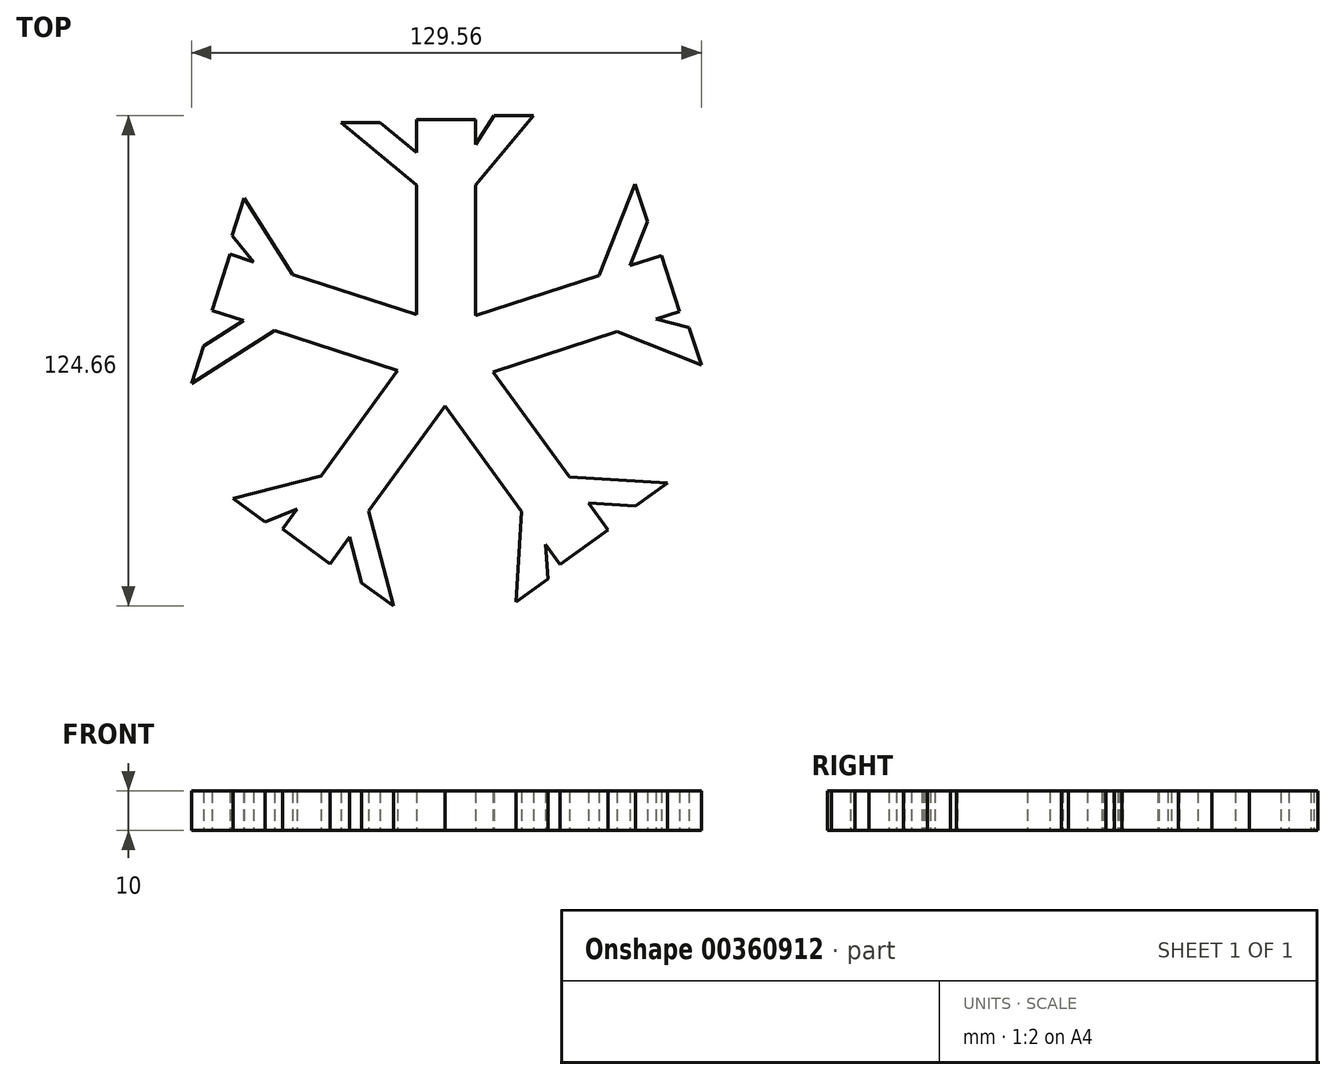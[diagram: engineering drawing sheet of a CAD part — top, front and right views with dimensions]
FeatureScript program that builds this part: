
annotation { "Feature Type Name" : "Feature", "Feature Type Description" : "" }
export const myFeature = defineFeature(function(context is Context, id is Id, definition is map)
    precondition{}
    {
        {
            var Q0;
            Q0=qCreatedBy(makeId("Top.planeOp"),FACE);
            var sketch = newSketch(context, id + "F0", { "sketchPlane" : qUnion([Q0])});
            skLineSegment(sketch, "E0.bottom", {"start": v(-7.35, 60) * mm, "end": v(7.65, 60) * mm});
            skLineSegment(sketch, "E0.top", {"start": v(-7.35, 0) * mm, "end": v(7.65, 0) * mm});
            skLineSegment(sketch, "E0.left", {"start": v(-7.35, 60) * mm, "end": v(-7.35, 0) * mm});
            skLineSegment(sketch, "E0.right", {"start": v(7.65, 60) * mm, "end": v(7.65, 0) * mm});
            skLineSegment(sketch, "E1", {"start": v(7.65, 43.34) * mm, "end": v(22.3, 61.07) * mm});
            skLineSegment(sketch, "E2", {"start": v(22.3, 61.07) * mm, "end": v(12.3, 61.07) * mm});
            skLineSegment(sketch, "E3", {"start": v(12.3, 61.07) * mm, "end": v(7.65, 53.73) * mm});
            skLineSegment(sketch, "E4", {"start": v(-7.35, 43.34) * mm, "end": v(-26.63, 59.26) * mm});
            skLineSegment(sketch, "E5", {"start": v(-26.63, 59.26) * mm, "end": v(-16.62, 59.26) * mm});
            skLineSegment(sketch, "E6", {"start": v(-16.62, 59.26) * mm, "end": v(-9.92, 53.73) * mm});
            skLineSegment(sketch, "E7", {"start": v(-9.92, 53.73) * mm, "end": v(-6.99, 51.3) * mm});
            skPoint(sketch, "E7.endSnap0", {"position": v(-17, 51.3) * mm});
            skLineSegment(sketch, "E8.1.0", {"start": v(-59.34, 11.55) * mm, "end": v(-2.27, -7) * mm});
            skLineSegment(sketch, "E8.1.1", {"start": v(-2.27, -7) * mm, "end": v(2.36, 7.27) * mm});
            skLineSegment(sketch, "E8.1.2", {"start": v(-54.7, 25.81) * mm, "end": v(2.36, 7.27) * mm});
            skLineSegment(sketch, "E8.1.3", {"start": v(-38.85, 20.66) * mm, "end": v(-51.2, 40.08) * mm});
            skLineSegment(sketch, "E8.1.4", {"start": v(-51.2, 40.08) * mm, "end": v(-54.28, 30.56) * mm});
            skLineSegment(sketch, "E8.1.5", {"start": v(-54.28, 30.56) * mm, "end": v(-48.73, 23.87) * mm});
            skLineSegment(sketch, "E8.1.6", {"start": v(-43.49, 6.4) * mm, "end": v(-64.59, -7.01) * mm});
            skLineSegment(sketch, "E8.1.7", {"start": v(-64.59, -7.01) * mm, "end": v(-61.5, 2.5) * mm});
            skLineSegment(sketch, "E8.1.8", {"start": v(-61.5, 2.5) * mm, "end": v(-54.16, 7.16) * mm});
            skLineSegment(sketch, "E8.1.9", {"start": v(-59.34, 11.55) * mm, "end": v(-54.7, 25.81) * mm});
            skPoint(sketch, "E8.1.10", {"position": v(-54.04, -0.3) * mm});
            skLineSegment(sketch, "E8.1.11", {"start": v(-54.16, 7.16) * mm, "end": v(-50.95, 9.2) * mm});
            skLineSegment(sketch, "E8.2.0", {"start": v(-29.32, -52.86) * mm, "end": v(5.95, -4.32) * mm});
            skLineSegment(sketch, "E8.2.1", {"start": v(5.95, -4.32) * mm, "end": v(-6.19, 4.5) * mm});
            skLineSegment(sketch, "E8.2.2", {"start": v(-41.45, -44.05) * mm, "end": v(-6.19, 4.5) * mm});
            skLineSegment(sketch, "E8.2.3", {"start": v(-31.66, -30.57) * mm, "end": v(-53.93, -36.3) * mm});
            skLineSegment(sketch, "E8.2.4", {"start": v(-53.93, -36.3) * mm, "end": v(-45.84, -42.18) * mm});
            skLineSegment(sketch, "E8.2.5", {"start": v(-45.84, -42.18) * mm, "end": v(-37.76, -38.97) * mm});
            skLineSegment(sketch, "E8.2.6", {"start": v(-19.52, -39.38) * mm, "end": v(-13.3, -63.6) * mm});
            skLineSegment(sketch, "E8.2.7", {"start": v(-13.3, -63.6) * mm, "end": v(-21.38, -57.71) * mm});
            skLineSegment(sketch, "E8.2.8", {"start": v(-21.38, -57.71) * mm, "end": v(-23.55, -49.3) * mm});
            skLineSegment(sketch, "E8.2.9", {"start": v(-29.32, -52.86) * mm, "end": v(-41.45, -44.05) * mm});
            skPoint(sketch, "E8.2.10", {"position": v(-16.4, -51.49) * mm});
            skLineSegment(sketch, "E8.2.11", {"start": v(-23.55, -49.3) * mm, "end": v(-24.5, -45.6) * mm});
            skLineSegment(sketch, "E8.3.0", {"start": v(41.22, -44.22) * mm, "end": v(5.95, 4.32) * mm});
            skLineSegment(sketch, "E8.3.1", {"start": v(5.95, 4.32) * mm, "end": v(-6.19, -4.5) * mm});
            skLineSegment(sketch, "E8.3.2", {"start": v(29.08, -53.04) * mm, "end": v(-6.19, -4.5) * mm});
            skLineSegment(sketch, "E8.3.3", {"start": v(19.29, -39.55) * mm, "end": v(17.86, -62.51) * mm});
            skLineSegment(sketch, "E8.3.4", {"start": v(17.86, -62.51) * mm, "end": v(25.95, -56.63) * mm});
            skLineSegment(sketch, "E8.3.5", {"start": v(25.95, -56.63) * mm, "end": v(25.4, -47.96) * mm});
            skLineSegment(sketch, "E8.3.6", {"start": v(31.42, -30.74) * mm, "end": v(56.37, -32.3) * mm});
            skLineSegment(sketch, "E8.3.7", {"start": v(56.37, -32.3) * mm, "end": v(48.28, -38.17) * mm});
            skLineSegment(sketch, "E8.3.8", {"start": v(48.28, -38.17) * mm, "end": v(39.6, -37.63) * mm});
            skLineSegment(sketch, "E8.3.9", {"start": v(41.22, -44.22) * mm, "end": v(29.08, -53.04) * mm});
            skPoint(sketch, "E8.3.10", {"position": v(43.9, -31.51) * mm});
            skLineSegment(sketch, "E8.3.11", {"start": v(39.6, -37.63) * mm, "end": v(35.8, -37.4) * mm});
            skLineSegment(sketch, "E8.4.0", {"start": v(54.8, 25.54) * mm, "end": v(-2.27, 7) * mm});
            skLineSegment(sketch, "E8.4.1", {"start": v(-2.27, 7) * mm, "end": v(2.36, -7.27) * mm});
            skLineSegment(sketch, "E8.4.2", {"start": v(59.43, 11.27) * mm, "end": v(2.36, -7.27) * mm});
            skLineSegment(sketch, "E8.4.3", {"start": v(43.58, 6.12) * mm, "end": v(64.97, -2.33) * mm});
            skLineSegment(sketch, "E8.4.4", {"start": v(64.97, -2.33) * mm, "end": v(61.88, 7.18) * mm});
            skLineSegment(sketch, "E8.4.5", {"start": v(61.88, 7.18) * mm, "end": v(53.46, 9.33) * mm});
            skLineSegment(sketch, "E8.4.6", {"start": v(38.94, 20.39) * mm, "end": v(48.13, 43.64) * mm});
            skLineSegment(sketch, "E8.4.7", {"start": v(48.13, 43.64) * mm, "end": v(51.22, 34.12) * mm});
            skLineSegment(sketch, "E8.4.8", {"start": v(51.22, 34.12) * mm, "end": v(48.03, 26.04) * mm});
            skLineSegment(sketch, "E8.4.9", {"start": v(54.8, 25.54) * mm, "end": v(59.43, 11.27) * mm});
            skPoint(sketch, "E8.4.10", {"position": v(43.54, 32.01) * mm});
            skLineSegment(sketch, "E8.4.11", {"start": v(48.03, 26.04) * mm, "end": v(46.63, 22.5) * mm});
            skPoint(sketch, "E8.center", {"position": v(0, 0) * mm});
            skSolve(sketch);
        }
        {
            var Q0;
            {var subQ3=sQuery(id+"F0.wireOp",EDGE,"E0.bottom");Q0=makeQuery(id+"F0.imprint","IMPRINT",FACE,{"disambiguationData":[TD([[makeQuery(id+"F0.imprint","IMPRINT",EDGE,{"derivedFrom":subQ3}),-1.0]])]});}
            var Q1;
            {var subQ4=sQuery(id+"F0.wireOp",EDGE,"E8.1.9");Q1=makeQuery(id+"F0.imprint","IMPRINT",FACE,{"disambiguationData":[TD([[makeQuery(id+"F0.imprint","IMPRINT",EDGE,{"derivedFrom":subQ4}),-1.0]])]});}
            var Q2;
            {var subQ5=sQuery(id+"F0.wireOp",EDGE,"E8.2.9");Q2=makeQuery(id+"F0.imprint","IMPRINT",FACE,{"disambiguationData":[TD([[makeQuery(id+"F0.imprint","IMPRINT",EDGE,{"derivedFrom":subQ5}),-1.0]])]});}
            var Q3;
            {var subQ5=sQuery(id+"F0.wireOp",EDGE,"E8.3.9");Q3=makeQuery(id+"F0.imprint","IMPRINT",FACE,{"disambiguationData":[TD([[makeQuery(id+"F0.imprint","IMPRINT",EDGE,{"derivedFrom":subQ5}),-1.0]])]});}
            var Q4;
            {var subQ0=sQuery(id+"F0.wireOp",EDGE,"E8.4.9");Q4=makeQuery(id+"F0.imprint","IMPRINT",FACE,{"disambiguationData":[TD([[makeQuery(id+"F0.imprint","IMPRINT",EDGE,{"derivedFrom":subQ0}),-1.0]])]});}
            var Q5;
            {var subQ1=sQuery(id+"F0.wireOp",EDGE,"E8.4.6");Q5=makeQuery(id+"F0.imprint","IMPRINT",FACE,{"disambiguationData":[TD([[makeQuery(id+"F0.imprint","IMPRINT",EDGE,{"derivedFrom":subQ1}),-1.0]])]});}
            var Q6;
            {var subQ0=sQuery(id+"F0.wireOp",EDGE,"E8.4.3");Q6=makeQuery(id+"F0.imprint","IMPRINT",FACE,{"disambiguationData":[TD([[makeQuery(id+"F0.imprint","IMPRINT",EDGE,{"derivedFrom":subQ0}),1.0]])]});}
            var Q7;
            {var subQ0=sQuery(id+"F0.wireOp",EDGE,"E1");Q7=makeQuery(id+"F0.imprint","IMPRINT",FACE,{"disambiguationData":[TD([[makeQuery(id+"F0.imprint","IMPRINT",EDGE,{"derivedFrom":subQ0}),1.0]])]});}
            var Q8;
            {var subQ1=sQuery(id+"F0.wireOp",EDGE,"E4");Q8=makeQuery(id+"F0.imprint","IMPRINT",FACE,{"disambiguationData":[TD([[makeQuery(id+"F0.imprint","IMPRINT",EDGE,{"derivedFrom":subQ1}),-1.0]])]});}
            var Q9;
            {var subQ0=sQuery(id+"F0.wireOp",EDGE,"E8.1.3");Q9=makeQuery(id+"F0.imprint","IMPRINT",FACE,{"disambiguationData":[TD([[makeQuery(id+"F0.imprint","IMPRINT",EDGE,{"derivedFrom":subQ0}),1.0]])]});}
            var Q10;
            {var subQ1=sQuery(id+"F0.wireOp",EDGE,"E8.1.6");Q10=makeQuery(id+"F0.imprint","IMPRINT",FACE,{"disambiguationData":[TD([[makeQuery(id+"F0.imprint","IMPRINT",EDGE,{"derivedFrom":subQ1}),-1.0]])]});}
            var Q11;
            {var subQ0=sQuery(id+"F0.wireOp",EDGE,"E8.2.3");Q11=makeQuery(id+"F0.imprint","IMPRINT",FACE,{"disambiguationData":[TD([[makeQuery(id+"F0.imprint","IMPRINT",EDGE,{"derivedFrom":subQ0}),1.0]])]});}
            var Q12;
            {var subQ1=sQuery(id+"F0.wireOp",EDGE,"E8.2.6");Q12=makeQuery(id+"F0.imprint","IMPRINT",FACE,{"disambiguationData":[TD([[makeQuery(id+"F0.imprint","IMPRINT",EDGE,{"derivedFrom":subQ1}),-1.0]])]});}
            var Q13;
            {var subQ0=sQuery(id+"F0.wireOp",EDGE,"E8.3.3");Q13=makeQuery(id+"F0.imprint","IMPRINT",FACE,{"disambiguationData":[TD([[makeQuery(id+"F0.imprint","IMPRINT",EDGE,{"derivedFrom":subQ0}),1.0]])]});}
            var Q14;
            {var subQ1=sQuery(id+"F0.wireOp",EDGE,"E8.3.6");Q14=makeQuery(id+"F0.imprint","IMPRINT",FACE,{"disambiguationData":[TD([[makeQuery(id+"F0.imprint","IMPRINT",EDGE,{"derivedFrom":subQ1}),-1.0]])]});}
            var Q15;
            {var subQ3=sQuery(id+"F0.wireOp",EDGE,"E0.top");var subQ5=sQuery(id+"F0.wireOp",EDGE,"E0.right");var subQ6=makeQuery(id+"F0.imprint","INTERSECT",VERTEX,{"derivedFrom":[subQ3,subQ5]});Q15=makeQuery(id+"F0.imprint","IMPRINT",FACE,{"disambiguationData":[TD([[makeQuery(id+"F0.imprint","IMPRINT",EDGE,{"disambiguationData":[TD([[subQ6,1.0]])],"derivedFrom":subQ5}),1.0]])]});}
            var Q16;
            {var subQ0=sQuery(id+"F0.wireOp",EDGE,"E8.2.1");var subQ1=sQuery(id+"F0.wireOp",EDGE,"E8.2.0");var subQ2=makeQuery(id+"F0.imprint","INTERSECT",VERTEX,{"derivedFrom":[subQ1,subQ0]});Q16=makeQuery(id+"F0.imprint","IMPRINT",FACE,{"disambiguationData":[TD([[makeQuery(id+"F0.imprint","IMPRINT",EDGE,{"disambiguationData":[TD([[subQ2,1.0]])],"derivedFrom":subQ1}),1.0]])]});}
            var Q17;
            {var subQ5=sQuery(id+"F0.wireOp",EDGE,"E8.1.0");var subQ7=sQuery(id+"F0.wireOp",EDGE,"E8.1.1");var subQ8=makeQuery(id+"F0.imprint","INTERSECT",VERTEX,{"derivedFrom":[subQ5,subQ7]});Q17=makeQuery(id+"F0.imprint","IMPRINT",FACE,{"disambiguationData":[TD([[makeQuery(id+"F0.imprint","IMPRINT",EDGE,{"disambiguationData":[TD([[subQ8,1.0]])],"derivedFrom":subQ5}),-1.0]])]});}
            var Q18;
            {var subQ0=sQuery(id+"F0.wireOp",EDGE,"E8.1.1");var subQ1=sQuery(id+"F0.wireOp",EDGE,"E8.1.0");var subQ2=makeQuery(id+"F0.imprint","INTERSECT",VERTEX,{"derivedFrom":[subQ1,subQ0]});Q18=makeQuery(id+"F0.imprint","IMPRINT",FACE,{"disambiguationData":[TD([[makeQuery(id+"F0.imprint","IMPRINT",EDGE,{"disambiguationData":[TD([[subQ2,1.0]])],"derivedFrom":subQ1}),1.0]])]});}
            var Q19;
            {var subQ3=sQuery(id+"F0.wireOp",EDGE,"E0.left");var subQ7=sQuery(id+"F0.wireOp",EDGE,"E0.top");var subQ8=makeQuery(id+"F0.imprint","INTERSECT",VERTEX,{"derivedFrom":[subQ7,subQ3]});Q19=makeQuery(id+"F0.imprint","IMPRINT",FACE,{"disambiguationData":[TD([[makeQuery(id+"F0.imprint","IMPRINT",EDGE,{"disambiguationData":[TD([[subQ8,1.0]])],"derivedFrom":subQ3}),-1.0]])]});}
            var Q20;
            {var subQ0=sQuery(id+"F0.wireOp",EDGE,"E8.1.2");var subQ1=sQuery(id+"F0.wireOp",EDGE,"E0.left");var subQ2=makeQuery(id+"F0.imprint","INTERSECT",VERTEX,{"derivedFrom":[subQ1,subQ0]});Q20=makeQuery(id+"F0.imprint","IMPRINT",FACE,{"disambiguationData":[TD([[makeQuery(id+"F0.imprint","IMPRINT",EDGE,{"disambiguationData":[TD([[subQ2,-1.0]])],"derivedFrom":subQ1}),1.0]])]});}
            var Q21;
            {var subQ0=sQuery(id+"F0.wireOp",EDGE,"E8.1.2");var subQ1=sQuery(id+"F0.wireOp",EDGE,"E8.1.1");var subQ2=makeQuery(id+"F0.imprint","INTERSECT",VERTEX,{"derivedFrom":[subQ1,subQ0]});Q21=makeQuery(id+"F0.imprint","IMPRINT",FACE,{"disambiguationData":[TD([[makeQuery(id+"F0.imprint","IMPRINT",EDGE,{"disambiguationData":[TD([[subQ2,1.0]])],"derivedFrom":subQ0}),-1.0]])]});}
            var Q22;
            {var subQ3=sQuery(id+"F0.wireOp",EDGE,"E0.right");var subQ8=sQuery(id+"F0.wireOp",EDGE,"E8.4.0");var subQ11=makeQuery(id+"F0.imprint","INTERSECT",VERTEX,{"derivedFrom":[subQ3,subQ8]});Q22=makeQuery(id+"F0.imprint","IMPRINT",FACE,{"disambiguationData":[TD([[makeQuery(id+"F0.imprint","IMPRINT",EDGE,{"disambiguationData":[TD([[subQ11,-1.0]])],"derivedFrom":subQ3}),-1.0]])]});}
            var Q23;
            {var subQ0=sQuery(id+"F0.wireOp",EDGE,"E0.right");var subQ1=sQuery(id+"F0.wireOp",EDGE,"E0.top");var subQ2=makeQuery(id+"F0.imprint","INTERSECT",VERTEX,{"derivedFrom":[subQ1,subQ0]});Q23=makeQuery(id+"F0.imprint","IMPRINT",FACE,{"disambiguationData":[TD([[makeQuery(id+"F0.imprint","IMPRINT",EDGE,{"disambiguationData":[TD([[subQ2,1.0]])],"derivedFrom":subQ0}),-1.0]])]});}
            var Q24;
            {var subQ0=sQuery(id+"F0.wireOp",EDGE,"E0.left");var subQ1=sQuery(id+"F0.wireOp",EDGE,"E0.top");var subQ2=makeQuery(id+"F0.imprint","INTERSECT",VERTEX,{"derivedFrom":[subQ1,subQ0]});Q24=makeQuery(id+"F0.imprint","IMPRINT",FACE,{"disambiguationData":[TD([[makeQuery(id+"F0.imprint","IMPRINT",EDGE,{"disambiguationData":[TD([[subQ2,1.0]])],"derivedFrom":subQ0}),1.0]])]});}
            extrude(context, id + "F1", {"entities" : qUnion([Q0, Q1, Q2, Q3, Q4, Q5, Q6, Q7, Q8, Q9, Q10, Q11, Q12, Q13, Q14, Q15, Q16, Q17, Q18, Q19, Q20, Q21, Q22, Q23, Q24]), "depth" : 10 * mm});
        }
    });
